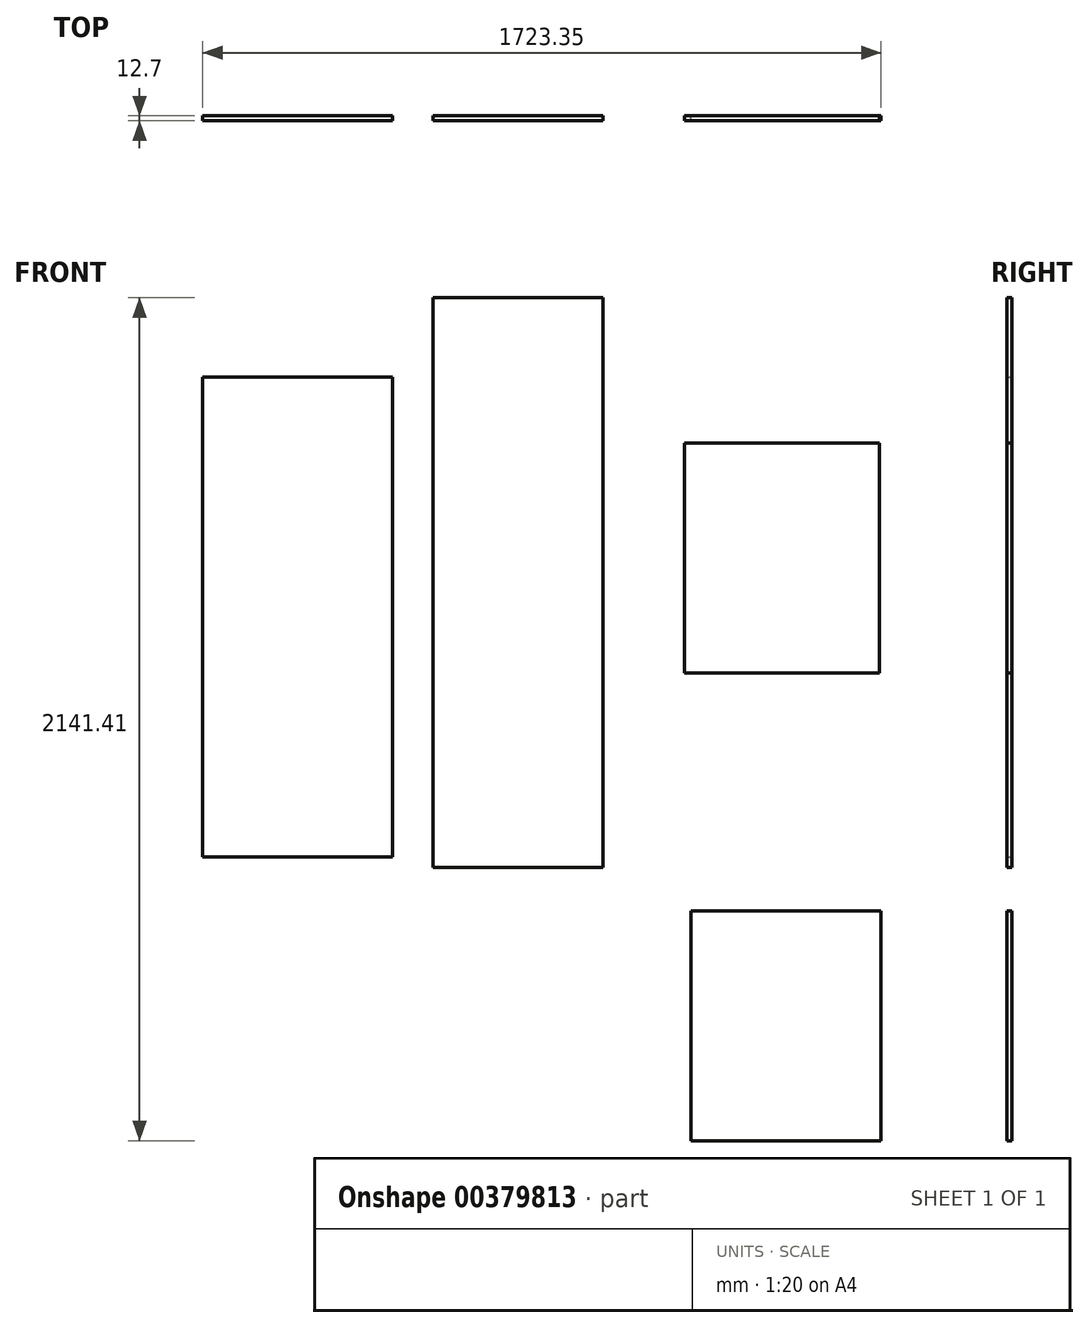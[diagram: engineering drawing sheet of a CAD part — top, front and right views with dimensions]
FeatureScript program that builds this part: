
annotation { "Feature Type Name" : "Feature", "Feature Type Description" : "" }
export const myFeature = defineFeature(function(context is Context, id is Id, definition is map)
    precondition{}
    {
        {
            var Q0;
            Q0=qCreatedBy(makeId("Front.planeOp"),FACE);
            var sketch = newSketch(context, id + "F0", { "sketchPlane" : qUnion([Q0])});
            skLineSegment(sketch, "E0.bottom", {"start": v(-823.55, 734.24) * mm, "end": v(-340.95, 734.24) * mm});
            skLineSegment(sketch, "E0.top", {"start": v(-823.55, -484.96) * mm, "end": v(-340.95, -484.96) * mm});
            skLineSegment(sketch, "E0.left", {"start": v(-823.55, 734.24) * mm, "end": v(-823.55, -484.96) * mm});
            skLineSegment(sketch, "E0.right", {"start": v(-340.95, 734.24) * mm, "end": v(-340.95, -484.96) * mm});
            skLineSegment(sketch, "E1.bottom", {"start": v(-238.77, 936.11) * mm, "end": v(193.03, 936.11) * mm});
            skLineSegment(sketch, "E1.top", {"start": v(-238.77, -511.69) * mm, "end": v(193.03, -511.69) * mm});
            skLineSegment(sketch, "E1.left", {"start": v(-238.77, 936.11) * mm, "end": v(-238.77, -511.69) * mm});
            skLineSegment(sketch, "E1.right", {"start": v(193.03, 936.11) * mm, "end": v(193.03, -511.69) * mm});
            skLineSegment(sketch, "E2.bottom", {"start": v(401.02, 567.7) * mm, "end": v(896.32, 567.7) * mm});
            skLineSegment(sketch, "E2.top", {"start": v(401.02, -16.5) * mm, "end": v(896.32, -16.5) * mm});
            skLineSegment(sketch, "E2.left", {"start": v(401.02, 567.7) * mm, "end": v(401.02, -16.5) * mm});
            skLineSegment(sketch, "E2.right", {"start": v(896.32, 567.7) * mm, "end": v(896.32, -16.5) * mm});
            skLineSegment(sketch, "E3.bottom", {"start": v(417.2, -621.1) * mm, "end": v(899.8, -621.1) * mm});
            skLineSegment(sketch, "E3.top", {"start": v(417.2, -1205.3) * mm, "end": v(899.8, -1205.3) * mm});
            skLineSegment(sketch, "E3.left", {"start": v(417.2, -621.1) * mm, "end": v(417.2, -1205.3) * mm});
            skLineSegment(sketch, "E3.right", {"start": v(899.8, -621.1) * mm, "end": v(899.8, -1205.3) * mm});
            skSolve(sketch);
        }
        {
            var Q0;
            Q0 = qSketchRegion(id + "F0", true);
            extrude(context, id + "F1", {"entities" : qUnion([Q0]), "depth" : 12.7 * mm});
        }
    });
